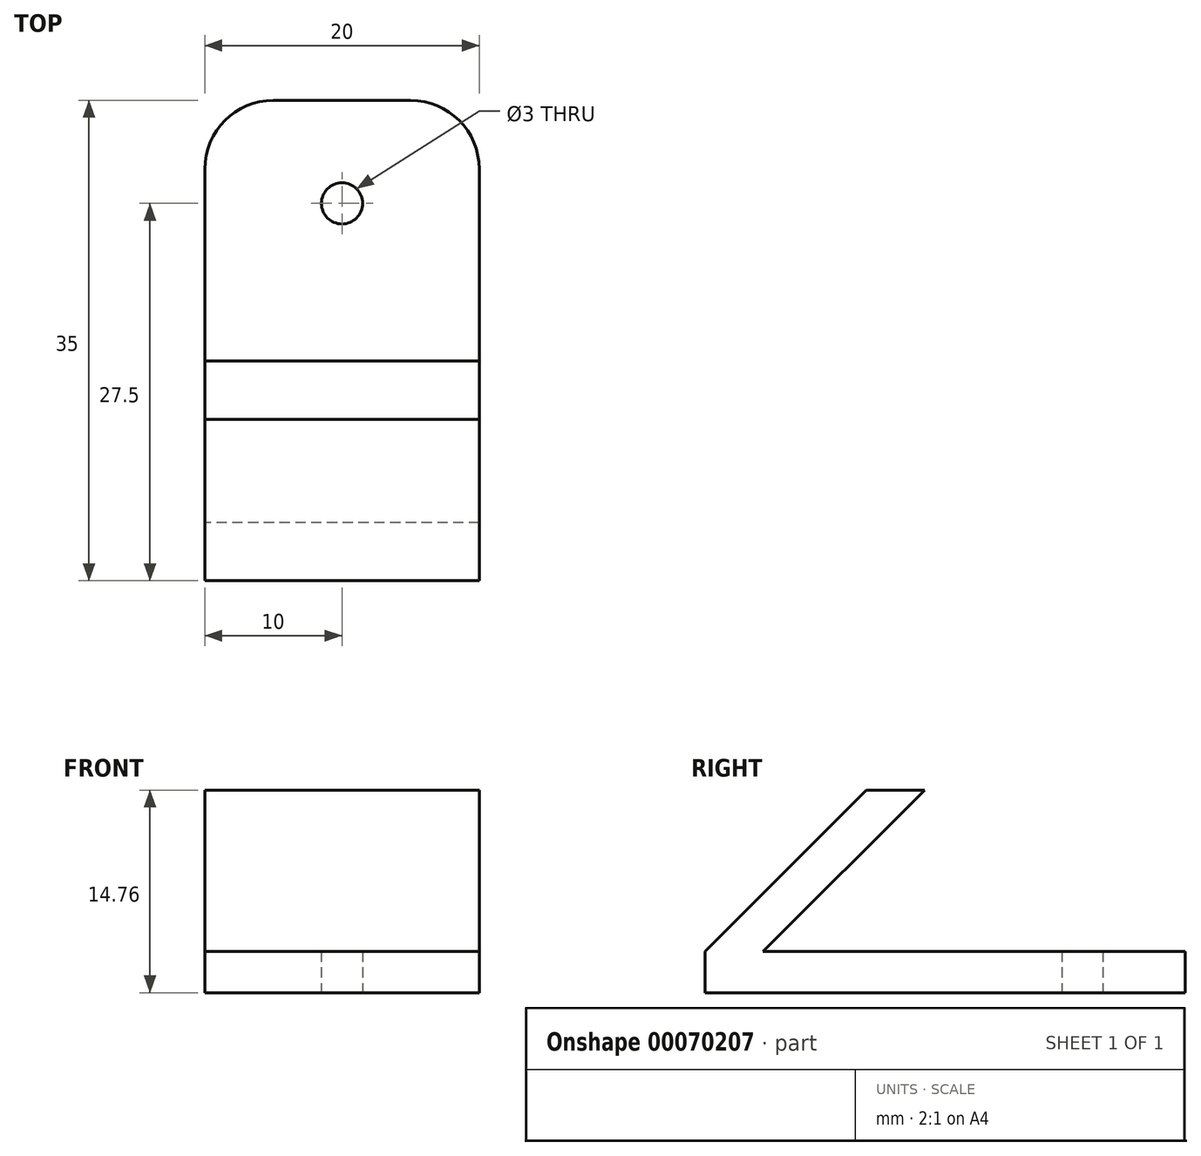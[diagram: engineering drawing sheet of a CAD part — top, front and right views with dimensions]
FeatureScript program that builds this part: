
annotation { "Feature Type Name" : "Feature", "Feature Type Description" : "" }
export const myFeature = defineFeature(function(context is Context, id is Id, definition is map)
    precondition{}
    {
        {
            var Q0;
            Q0=qCreatedBy(makeId("Right.planeOp"),FACE);
            var sketch = newSketch(context, id + "F0", { "sketchPlane" : qUnion([Q0])});
            skLineSegment(sketch, "E0", {"start": v(0, 14.76) * mm, "end": v(-11.76, 3) * mm});
            skLineSegment(sketch, "E1", {"start": v(-11.76, 3) * mm, "end": v(19, 3) * mm});
            skLineSegment(sketch, "E2", {"start": v(19, 3) * mm, "end": v(19, 0) * mm});
            skLineSegment(sketch, "E3", {"start": v(19, 0) * mm, "end": v(-19, 0) * mm});
            skLineSegment(sketch, "E4", {"start": v(-19, 0) * mm, "end": v(-4.24, 14.76) * mm});
            skLineSegment(sketch, "E5", {"start": v(-4.24, 14.76) * mm, "end": v(0, 14.76) * mm});
            skLineSegment(sketch, "E6", {"start": v(-16, 3) * mm, "end": v(-16, 0) * mm});
            skSolve(sketch);
        }
        {
            var Q0;
            Q0=makeQuery(id+"F0.imprint","IMPRINT",FACE,{"disambiguationData":[TD([[makeQuery(id+"F0.imprint","IMPRINT",EDGE,{"derivedFrom":sQuery(id+"F0.wireOp",EDGE,"E0")}),-1.0]])]});
            extrude(context, id + "F1", {"entities" : qUnion([Q0]), "depth" : 20 * mm, "offsetDistance" : 25 * mm, "symmetric" : true});
        }
        {
            var Q0;
            Q0=makeQuery(id+"F1.opExtrude","CAP_EDGE",EDGE,{"disambiguationData":[OSD([sQuery(id+"F0.wireOp",EDGE,"E2")])],"isStart":false});
            var Q1;
            Q1=makeQuery(id+"F1.opExtrude","CAP_EDGE",EDGE,{"disambiguationData":[OSD([sQuery(id+"F0.wireOp",EDGE,"E2")])],"isStart":true});
            fillet(context, id + "F2", {"entities" : qUnion([Q0, Q1]), "radius" : 5 * mm, "tangentPropagation" : true, "allowEdgeOverflow" : false});
        }
        {
            var Q0;
            Q0=makeQuery(id+"F1.opExtrude","SWEPT_FACE",FACE,{"disambiguationData":[OSD([sQuery(id+"F0.wireOp",EDGE,"E3")])]});
            var sketch = newSketch(context, id + "F3", { "sketchPlane" : qUnion([Q0])});
            skPoint(sketch, "E7", {"position": v(0, -11.5) * mm});
            skPoint(sketch, "E7.positionSnap0", {"position": v(0, -19) * mm});
            skSolve(sketch);
        }
        {
            var Q0;
            Q0=sQuery(id+"F3.wireOp",VERTEX,"E7");
            var Q1;
            Q1=makeQuery(id+"F1.opExtrude","SWEPT_BODY",BODY,{"disambiguationData":[OSD([sQuery(id+"F0.wireOp",EDGE,"E0"),sQuery(id+"F0.wireOp",EDGE,"E1"),sQuery(id+"F0.wireOp",EDGE,"E2"),sQuery(id+"F0.wireOp",EDGE,"E3"),sQuery(id+"F0.wireOp",EDGE,"E4"),sQuery(id+"F0.wireOp",EDGE,"E5"),sQuery(id+"F0.wireOp",EDGE,"E6")])]});
            hole(context, id + "F4", {"style" : HoleStyle.SIMPLE, "endStyle" : HoleEndStyle.THROUGH, "holeDiameter" : 3 * mm, "majorDiameter" : 5 * mm, "isTappedThrough" : true, "tappedDepth" : 12 * mm, "tapClearance" : 3, "locations" : qUnion([Q0]), "scope" : qUnion([Q1])});
        }
    });
